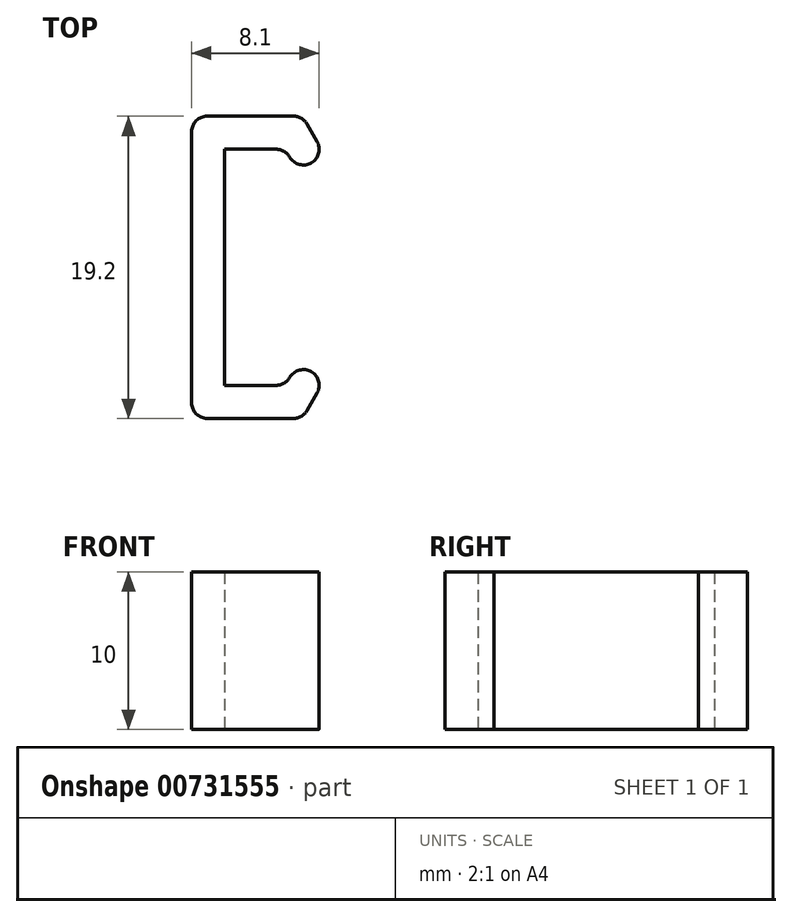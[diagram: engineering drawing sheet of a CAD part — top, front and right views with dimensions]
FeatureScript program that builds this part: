
annotation { "Feature Type Name" : "Feature", "Feature Type Description" : "" }
export const myFeature = defineFeature(function(context is Context, id is Id, definition is map)
    precondition{}
    {
        {
            var Q0;
            Q0=qCreatedBy(makeId("Top.planeOp"),FACE);
            var sketch = newSketch(context, id + "F0", { "sketchPlane" : qUnion([Q0])});
            skLineSegment(sketch, "E0.bottom", {"start": v(-2.5, 7.5) * mm, "end": v(0.77, 7.5) * mm});
            skLineSegment(sketch, "E0.top", {"start": v(-2.5, -7.5) * mm, "end": v(0.77, -7.5) * mm});
            skLineSegment(sketch, "E0.left", {"start": v(-2.5, 7.5) * mm, "end": v(-2.5, -7.5) * mm});
            skLineSegment(sketch, "E1", {"start": v(-2.5, 0) * mm, "end": v(0, 0) * mm, "construction": true});
            skLineSegment(sketch, "E2", {"start": v(0, 0) * mm, "end": v(2.5, 0) * mm, "construction": true});
            skLineSegment(sketch, "E3", {"start": v(0, 0) * mm, "end": v(0, -7.5) * mm, "construction": true});
            skLineSegment(sketch, "E4", {"start": v(0, 0) * mm, "end": v(0, 7.5) * mm, "construction": true});
            skLineSegment(sketch, "E5", {"start": v(1.86, 9.6) * mm, "end": v(-3.6, 9.6) * mm});
            skLineSegment(sketch, "E6", {"start": v(-4.6, 8.6) * mm, "end": v(-4.6, -8.6) * mm});
            skLineSegment(sketch, "E7", {"start": v(-3.6, -9.6) * mm, "end": v(1.86, -9.6) * mm});
            skArc(sketch, "E8", {"start": v(1.63, 7) * mm, "mid": v(3, 6.63) * mm, "end": v(3.37, 8) * mm});
            skArc(sketch, "E9", {"start": v(3.37, -8) * mm, "mid": v(3, -6.63) * mm, "end": v(1.63, -7) * mm});
            skLineSegment(sketch, "E10", {"start": v(2.73, 9.1) * mm, "end": v(3.37, 8) * mm});
            skLineSegment(sketch, "E11", {"start": v(2.73, -9.1) * mm, "end": v(3.37, -8) * mm});
            skPoint(sketch, "E12.visualSharp", {"position": v(2.44, 9.6) * mm});
            skArc(sketch, "E12.filletArc", {"start": v(2.73, 9.1) * mm, "mid": v(2.36, 9.47) * mm, "end": v(1.86, 9.6) * mm});
            skPoint(sketch, "E13.visualSharp", {"position": v(1.5, 7.5) * mm});
            skArc(sketch, "E13.filletArc", {"start": v(1.63, 7) * mm, "mid": v(1.27, 7.37) * mm, "end": v(0.77, 7.5) * mm});
            skPoint(sketch, "E14.visualSharp", {"position": v(1.5, -7.5) * mm});
            skArc(sketch, "E14.filletArc", {"start": v(0.77, -7.5) * mm, "mid": v(1.27, -7.37) * mm, "end": v(1.63, -7) * mm});
            skPoint(sketch, "E15.visualSharp", {"position": v(-4.6, -9.6) * mm});
            skArc(sketch, "E15.filletArc", {"start": v(-4.6, -8.6) * mm, "mid": v(-4.3, -9.3) * mm, "end": v(-3.6, -9.6) * mm});
            skPoint(sketch, "E16.visualSharp", {"position": v(-4.6, 9.6) * mm});
            skArc(sketch, "E16.filletArc", {"start": v(-3.6, 9.6) * mm, "mid": v(-4.3, 9.3) * mm, "end": v(-4.6, 8.6) * mm});
            skLineSegment(sketch, "E17", {"start": v(2.5, 7.5) * mm, "end": v(2.5, -7.5) * mm, "construction": true});
            skPoint(sketch, "E18.visualSharp", {"position": v(2.44, -9.6) * mm});
            skArc(sketch, "E18.filletArc", {"start": v(1.86, -9.6) * mm, "mid": v(2.36, -9.47) * mm, "end": v(2.73, -9.1) * mm});
            skSolve(sketch);
        }
        {
            var Q0;
            Q0 = qSketchRegion(id + "F0", true);
            extrude(context, id + "F1", {"entities" : qUnion([Q0]), "depth" : 10 * mm, "offsetDistance" : 25 * mm});
        }
    });
